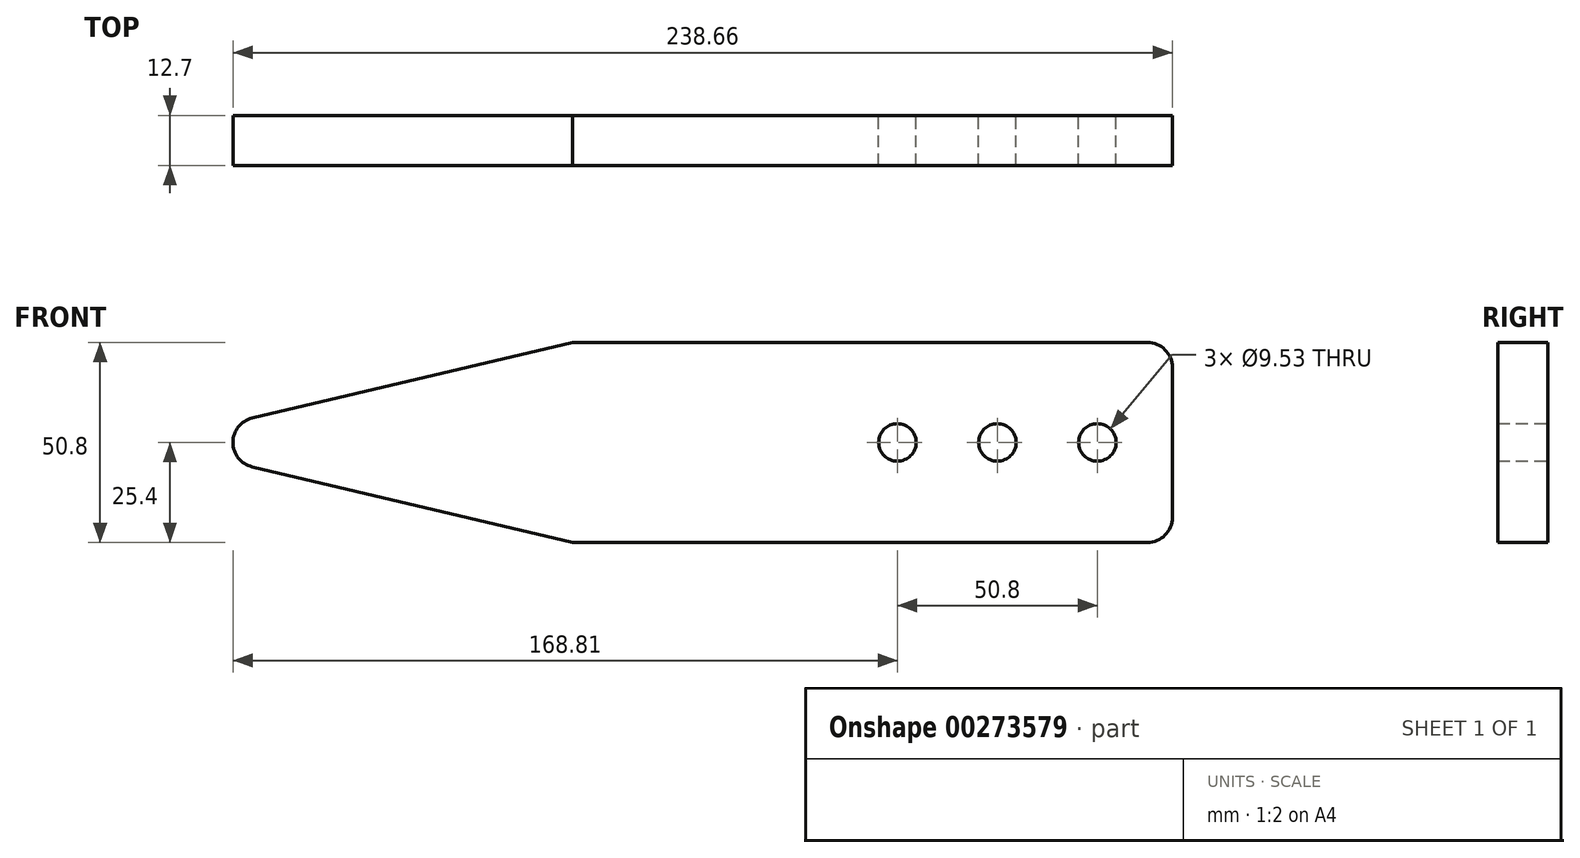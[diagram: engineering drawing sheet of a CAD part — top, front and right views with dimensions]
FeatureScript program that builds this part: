
annotation { "Feature Type Name" : "Feature", "Feature Type Description" : "" }
export const myFeature = defineFeature(function(context is Context, id is Id, definition is map)
    precondition{}
    {
        {
            var Q0;
            Q0=qCreatedBy(makeId("Front.planeOp"),FACE);
            var sketch = newSketch(context, id + "F0", { "sketchPlane" : qUnion([Q0])});
            skLineSegment(sketch, "E0.bottom", {"start": v(-76.2, 25.4) * mm, "end": v(76.2, 25.4) * mm});
            skLineSegment(sketch, "E0.top", {"start": v(-76.2, -25.4) * mm, "end": v(76.2, -25.4) * mm});
            skLineSegment(sketch, "E0.left", {"start": v(-76.2, 25.4) * mm, "end": v(-76.2, -25.4) * mm});
            skLineSegment(sketch, "E0.right", {"start": v(76.2, 25.4) * mm, "end": v(76.2, -25.4) * mm});
            skPoint(sketch, "E0.middle", {"position": v(0, 0) * mm});
            skCircle(sketch, "E1", {"center": v(57.15, 0) * mm, "radius": 4.76 * mm});
            skCircle(sketch, "E2", {"center": v(31.75, 0) * mm, "radius": 4.76 * mm});
            skCircle(sketch, "E3", {"center": v(6.35, 0) * mm, "radius": 4.76 * mm});
            skLineSegment(sketch, "E4", {"start": v(-76.2, 25.4) * mm, "end": v(-183.73, 0) * mm});
            skLineSegment(sketch, "E5", {"start": v(-183.73, 0) * mm, "end": v(-76.2, -25.4) * mm});
            skSolve(sketch);
        }
        {
            var Q0;
            Q0 = qSketchRegion(id + "F0", true);
            extrude(context, id + "F1", {"entities" : qUnion([Q0]), "endBound" : BoundingType.SYMMETRIC, "depth" : 12.7 * mm});
        }
        {
            var Q0;
            Q0=makeQuery(id+"F1.opExtrude","SWEPT_EDGE",EDGE,{"disambiguationData":[OSD([sQuery(id+"F0.wireOp",EDGE,"E4"),sQuery(id+"F0.wireOp",EDGE,"E5")])]});
            var Q1;
            Q1=makeQuery(id+"F1.opExtrude","SWEPT_EDGE",EDGE,{"disambiguationData":[OSD([sQuery(id+"F0.wireOp",EDGE,"E0.bottom"),sQuery(id+"F0.wireOp",EDGE,"E0.right")])]});
            var Q2;
            Q2=makeQuery(id+"F1.opExtrude","SWEPT_EDGE",EDGE,{"disambiguationData":[OSD([sQuery(id+"F0.wireOp",EDGE,"E0.top"),sQuery(id+"F0.wireOp",EDGE,"E0.right")])]});
            fillet(context, id + "F2", {"entities" : qUnion([Q0, Q1, Q2]), "radius" : 6.35 * mm, "tangentPropagation" : true, "allowEdgeOverflow" : false});
        }
    });
